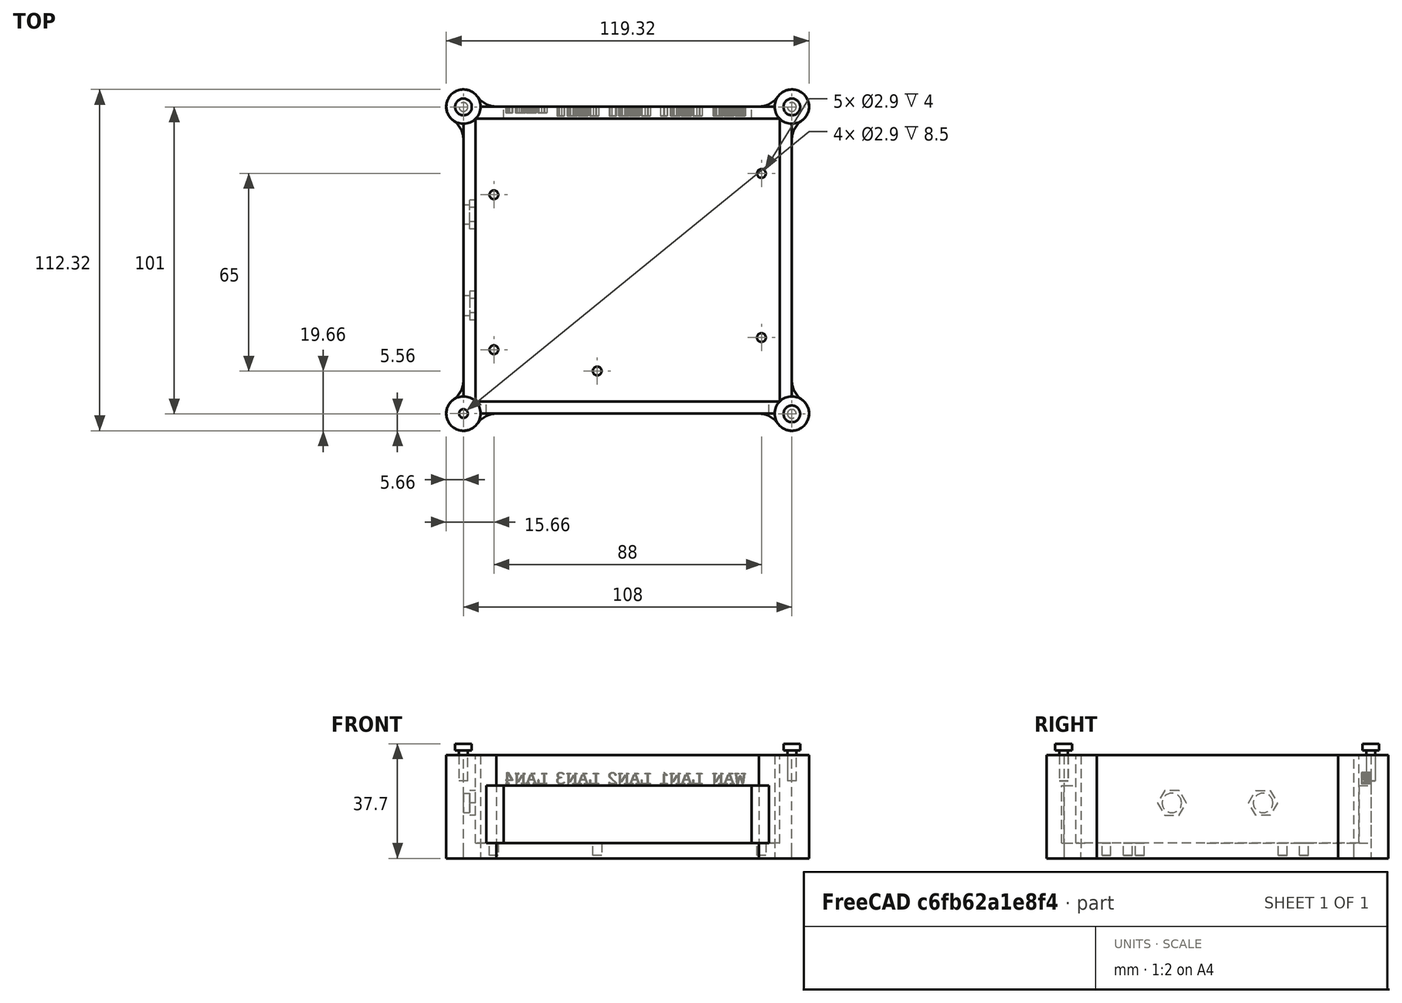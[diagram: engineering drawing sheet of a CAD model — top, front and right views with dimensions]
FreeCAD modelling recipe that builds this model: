
FCSTD DOCUMENT  (FreeCAD 2023.521R14555 (Git shallow))
Label: HLK-7628N_case
License: All rights reserved
objects: PartDesign::SubShapeBinder×13, Sketcher::SketchObject×12, PartDesign::Pocket×10, PartDesign::Pad×8, PartDesign::Mirrored×6, PartDesign::Body×5, Part::Part2DObjectPython×5, PartDesign::FeatureBase×3, PartDesign::MultiTransform×2, PartDesign::Plane×2, PartDesign::Boolean×2
note: 137 computed .brp shape members not serialized (recipe doc carries the construction recipe); baked Part::Feature solids carry a one-line shape summary decoded from their .brp

FEATURE [Sketcher::SketchObject] Sketch
  ArcFitTolerance = 1e-06
  AttachmentSupport = -> [XY_Plane]
  ExternalBSplineMaxDegree = 5
  ExternalBSplineTolerance = 0.0001
  FullyConstrained = true
  InternalTolerance = 1e-06
  InvalidShape = false
  MakeInternals = false
  MapMode = 5
  Support = -> [XY_Plane]
  TreeRank = 11
  ValidateShape = true
  sketch-geometry (4):
    g0: LineSegment StartX=-50 StartY=46.5 StartZ=0 EndX=50 EndY=46.5 EndZ=0
    g1: LineSegment StartX=50 StartY=46.5 StartZ=0 EndX=50 EndY=-46.5 EndZ=0
    g2: LineSegment StartX=50 StartY=-46.5 StartZ=0 EndX=-50 EndY=-46.5 EndZ=0
    g3: LineSegment StartX=-50 StartY=-46.5 StartZ=0 EndX=-50 EndY=46.5 EndZ=0
  constraints (11):
    c: Coincident(g0,g1)
    c: Coincident(g1,g2)
    c: Coincident(g2,g3)
    c: Coincident(g3,g0)
    c: Horizontal(g0)
    c: Horizontal(g2)
    c: Vertical(g1)
    c: Vertical(g3)
    c: Symmetric(g0,g1,g-1)
    c: DistanceX(g2,g2) = 100
    c: DistanceY(g3,g3) = 93
FEATURE [PartDesign::Pad] Pad
  AddSubType = 0
  AlongSketchNormal = false
  AutoTaperInnerAngle = true
  CheckUpToFaceLimits = true
  ClaimChildren = false
  Direction = (0,0,1)
  Fit = 0
  FitJoin = 0
  InnerFit = 0
  InnerFitJoin = 0
  InvalidShape = false
  Length = 5
  Length2 = 100
  Linearize = true
  NewSolid = false
  Profile = -> Sketch
  Suppress = false
  TaperInnerAngle = 0
  TaperInnerAngleRev = 0
  TreeRank = 12
  Type = 0
  ValidateShape = true
  _ProfileBasedVersion = 1
FEATURE [Sketcher::SketchObject] Sketch001
  ArcFitTolerance = 1e-06
  AttachmentSupport = -> [Pad]
  ExternalBSplineMaxDegree = 5
  ExternalBSplineTolerance = 0.0001
  ExternalGeometry = -> [Pad]
  FullyConstrained = true
  InternalTolerance = 1e-06
  InvalidShape = false
  MakeInternals = false
  MapMode = 5
  Placement = pos=(0,0,0) rot=(1,0,0;3.14159rad)
  Support = -> [Pad]
  TreeRank = 13
  ValidateShape = true
  sketch-geometry (12):
    g0: LineSegment StartX=-54 StartY=-50.5 StartZ=0 EndX=54 EndY=-50.5 EndZ=0
    g1: LineSegment StartX=54 StartY=-50.5 StartZ=0 EndX=54 EndY=50.5 EndZ=0
    g2: LineSegment StartX=54 StartY=50.5 StartZ=0 EndX=-54 EndY=50.5 EndZ=0
    g3: LineSegment StartX=-54 StartY=50.5 StartZ=0 EndX=-54 EndY=-50.5 EndZ=0
    g4: LineSegment [constr] StartX=-50 StartY=46.5 StartZ=0 EndX=-50 EndY=50.5 EndZ=0
    g5: LineSegment [constr] StartX=-50 StartY=46.5 StartZ=0 EndX=-54 EndY=46.5 EndZ=0
    g6: LineSegment StartX=-50 StartY=-46.5 StartZ=0 EndX=50 EndY=-46.5 EndZ=0
    g7: LineSegment StartX=50 StartY=-46.5 StartZ=0 EndX=50 EndY=46.5 EndZ=0
    g8: LineSegment StartX=50 StartY=46.5 StartZ=0 EndX=-50 EndY=46.5 EndZ=0
    g9: LineSegment StartX=-50 StartY=46.5 StartZ=0 EndX=-50 EndY=-46.5 EndZ=0
    g10: LineSegment [constr] StartX=50 StartY=-46.5 StartZ=0 EndX=54 EndY=-46.5 EndZ=0
    g11: LineSegment [constr] StartX=50 StartY=-46.5 StartZ=0 EndX=50 EndY=-50.5 EndZ=0
  constraints (34):
    c: Coincident(g0,g1)
    c: Coincident(g1,g2)
    c: Coincident(g2,g3)
    c: Coincident(g3,g0)
    c: Horizontal(g0)
    c: Horizontal(g2)
    c: Vertical(g1)
    c: Vertical(g3)
    c: Coincident(g4,g-6)
    c: PointOnObject(g4,g2)
    c: Vertical(g4)
    c: Coincident(g5,g-6)
    c: PointOnObject(g5,g3)
    c: Horizontal(g5)
    c: Equal(g5,g4)
    c: Coincident(g6,g7)
    c: Coincident(g7,g8)
    c: Coincident(g8,g9)
    c: Coincident(g9,g6)
    c: Horizontal(g6)
    c: Horizontal(g8)
    c: Vertical(g7)
    c: Vertical(g9)
    c: Coincident(g6,g-5)
    c: Coincident(g7,g-6)
    c: DistanceX(g5,g5) = 4
    c: Coincident(g10,g6)
    c: PointOnObject(g10,g1)
    c: Horizontal(g10)
    c: Coincident(g11,g6)
    c: PointOnObject(g11,g0)
    c: Vertical(g11)
    c: Equal(g10,g11)
    c: Equal(g10,g4)
FEATURE [PartDesign::Pad] Pad001
  AddSubType = 0
  AlongSketchNormal = false
  AutoTaperInnerAngle = true
  BaseFeature = -> Pad
  CheckUpToFaceLimits = true
  ClaimChildren = false
  Direction = (0,0,-1)
  Fit = 0
  FitJoin = 0
  InnerFit = 0
  InnerFitJoin = 0
  InvalidShape = false
  Length = 34
  Length2 = 100
  Linearize = true
  NewSolid = false
  Profile = -> Sketch001
  Reversed = true
  Suppress = false
  TaperInnerAngle = 0
  TaperInnerAngleRev = 0
  TreeRank = 14
  Type = 0
  ValidateShape = true
  _ProfileBasedVersion = 1
FEATURE [Sketcher::SketchObject] Sketch002
  ArcFitTolerance = 1e-06
  AttachmentSupport = -> [Pad001]
  ExternalBSplineMaxDegree = 5
  ExternalBSplineTolerance = 0.0001
  ExternalGeometry = -> [Pad001]
  FullyConstrained = true
  InternalTolerance = 1e-06
  InvalidShape = false
  MakeInternals = false
  MapMode = 5
  Placement = pos=(0,46.5,0) rot=(1,0,0;1.5708rad)
  Support = -> [Pad001]
  TreeRank = 15
  ValidateShape = true
  sketch-geometry (4):
    g0: LineSegment StartX=40.75 StartY=5 StartZ=0 EndX=-40.75 EndY=5 EndZ=0
    g1: LineSegment StartX=-40.75 StartY=5 StartZ=0 EndX=-40.75 EndY=24 EndZ=0
    g2: LineSegment StartX=-40.75 StartY=24 StartZ=0 EndX=40.75 EndY=24 EndZ=0
    g3: LineSegment StartX=40.75 StartY=24 StartZ=0 EndX=40.75 EndY=5 EndZ=0
  constraints (11):
    c: Coincident(g0,g1)
    c: Coincident(g1,g2)
    c: Coincident(g2,g3)
    c: Coincident(g3,g0)
    c: Horizontal(g2)
    c: Vertical(g1)
    c: Vertical(g3)
    c: PointOnObject(g0,g-3)
    c: Symmetric(g0,g0,g-2)
    c: DistanceX(g0,g0) = 81.5
    c: DistanceY(g1,g1) = 19
FEATURE [PartDesign::Mirrored] Mirrored001
  AddSubType = 0
  CopyShape = false
  InvalidShape = false
  MirrorPlane = -> YZ_Plane
  NewSolid = false
  ParallelTransform = true
  SubTransform = true
  Suppress = false
  TreeRank = 27
  ValidateShape = true
  _Version = 3
FEATURE [PartDesign::Mirrored] Mirrored002
  AddSubType = 0
  CopyShape = false
  InvalidShape = false
  MirrorPlane = -> XZ_Plane
  NewSolid = false
  ParallelTransform = true
  SubTransform = true
  Suppress = false
  TreeRank = 28
  ValidateShape = true
  _Version = 3
FEATURE [Sketcher::SketchObject] Sketch008
  ArcFitTolerance = 1e-06
  AttachmentSupport = -> [XY_Plane001]
  ExternalBSplineMaxDegree = 5
  ExternalBSplineTolerance = 0.0001
  FullyConstrained = true
  InternalTolerance = 1e-06
  InvalidShape = false
  MakeInternals = false
  MapMode = 5
  Support = -> [XY_Plane001]
  TreeRank = 52
  ValidateShape = false
  sketch-geometry (1):
    g0: Circle CenterX=0 CenterY=0 CenterZ=0 NormalX=0 NormalY=0 NormalZ=1 AngleXU=0 Radius=1.45
  constraints (2):
    c: Coincident(g0,g-1)
    c: Diameter(g0) = 2.9
FEATURE [PartDesign::Pad] Pad004
  AddSubType = 0
  AlongSketchNormal = false
  AutoTaperInnerAngle = true
  CheckUpToFaceLimits = true
  ClaimChildren = false
  Direction = (0,0,1)
  Fit = 0
  FitJoin = 0
  InnerFit = 0
  InnerFitJoin = 0
  InvalidShape = false
  Length = 10
  Length2 = 10
  Linearize = true
  NewSolid = false
  Profile = -> Sketch008
  ReferenceAxis = -> Sketch008 [N_Axis]
  Suppress = false
  TaperInnerAngle = 0
  TaperInnerAngleRev = 0
  TreeRank = 53
  Type = 0
  ValidateShape = false
  _ProfileBasedVersion = 1
FEATURE [Sketcher::SketchObject] Sketch009
  ArcFitTolerance = 1e-06
  AttachmentSupport = -> [Pad004]
  ExternalBSplineMaxDegree = 5
  ExternalBSplineTolerance = 0.0001
  FullyConstrained = true
  InternalTolerance = 1e-06
  InvalidShape = false
  MakeInternals = false
  MapMode = 5
  Placement = pos=(0,0,10) rot=(0,0,1;0rad)
  Support = -> [Pad004]
  TreeRank = 54
  ValidateShape = false
  sketch-geometry (1):
    g0: Circle CenterX=0 CenterY=0 CenterZ=0 NormalX=0 NormalY=0 NormalZ=1 AngleXU=0 Radius=2.75
  constraints (2):
    c: Coincident(g0,g-1)
    c: Diameter(g0) = 5.5
FEATURE [PartDesign::Pad] Pad005
  AddSubType = 0
  AlongSketchNormal = false
  AutoTaperInnerAngle = true
  BaseFeature = -> Pad004
  CheckUpToFaceLimits = true
  ClaimChildren = false
  Direction = (0,0,1)
  Fit = 0
  FitJoin = 0
  InnerFit = 0
  InnerFitJoin = 0
  InvalidShape = false
  Length = 2.2
  Length2 = 10
  Linearize = true
  NewSolid = false
  Profile = -> Sketch009
  ReferenceAxis = -> Sketch009 [N_Axis]
  Suppress = false
  TaperInnerAngle = 0
  TaperInnerAngleRev = 0
  TreeRank = 55
  Type = 0
  ValidateShape = false
  _ProfileBasedVersion = 1
FEATURE [PartDesign::Body] Body001  label="M3_10"
  AutoGroupSolids = false
  ClaimAllChildren = false
  ExportMode = 0
  Group = -> [Sketch008,Pad004,Sketch009,Pad005]
  InvalidShape = false
  Origin = -> Origin001
  Placement = pos=(-54,-50.5,25.5) rot=(0,0,1;0rad)
  Tip = -> Pad005
  TreeRank = 56
  ValidateShape = false
  _ExportChildren = -> [Pad004,Pad005]
  _GroupVersion = 1
FEATURE [PartDesign::SubShapeBinder] Pocket006_Profile  label="Pocket006_Profile(WAN)"
  BindCopyOnChange = 0
  BindMode = 0
  ClaimChildren = false
  Context = -> Body [Pocket006_Profile.]
  EdgeTolerance = 1e-06
  FillStyle = 0
  Fuse = false
  InvalidShape = false
  MakeFace = true
  MergeEdges = true
  OffsetFill = false
  OffsetIntersection = false
  OffsetJoinType = 0
  OffsetOpenResult = false
  Outline = false
  PartialLoad = false
  Relative = true
  SplitEdges = false
  Support = -> [ShapeString]
  TightBound = false
  TreeRank = 74
  ValidateShape = false
  _Version = 8
FEATURE [PartDesign::SubShapeBinder] Pocket007_Profile  label="Pocket007_Profile(LAN1)"
  BindCopyOnChange = 0
  BindMode = 0
  ClaimChildren = false
  Context = -> Body [Pocket007_Profile.]
  EdgeTolerance = 1e-06
  FillStyle = 0
  Fuse = false
  InvalidShape = false
  MakeFace = true
  MergeEdges = true
  OffsetFill = false
  OffsetIntersection = false
  OffsetJoinType = 0
  OffsetOpenResult = false
  Outline = false
  PartialLoad = false
  Relative = true
  SplitEdges = false
  Support = -> [ShapeString001]
  TightBound = false
  TreeRank = 76
  ValidateShape = false
  _Version = 8
FEATURE [PartDesign::SubShapeBinder] Pocket008_Profile  label="Pocket008_Profile(LAN2)"
  BindCopyOnChange = 0
  BindMode = 0
  ClaimChildren = false
  Context = -> Body [Pocket008_Profile.]
  EdgeTolerance = 1e-06
  FillStyle = 0
  Fuse = false
  InvalidShape = false
  MakeFace = true
  MergeEdges = true
  OffsetFill = false
  OffsetIntersection = false
  OffsetJoinType = 0
  OffsetOpenResult = false
  Outline = false
  PartialLoad = false
  Relative = true
  SplitEdges = false
  Support = -> [ShapeString002]
  TightBound = false
  TreeRank = 78
  ValidateShape = false
  _Version = 8
FEATURE [PartDesign::SubShapeBinder] Pocket009_Profile  label="Pocket009_Profile(LAN3)"
  BindCopyOnChange = 0
  BindMode = 0
  ClaimChildren = false
  Context = -> Body [Pocket009_Profile.]
  EdgeTolerance = 1e-06
  FillStyle = 0
  Fuse = false
  InvalidShape = false
  MakeFace = true
  MergeEdges = true
  OffsetFill = false
  OffsetIntersection = false
  OffsetJoinType = 0
  OffsetOpenResult = false
  Outline = false
  PartialLoad = false
  Relative = true
  SplitEdges = false
  Support = -> [ShapeString003]
  TightBound = false
  TreeRank = 80
  ValidateShape = false
  _Version = 8
FEATURE [PartDesign::SubShapeBinder] Pocket010_Profile  label="Pocket010_Profile(LAN4)"
  BindCopyOnChange = 0
  BindMode = 0
  ClaimChildren = false
  Context = -> Body [Pocket010_Profile.]
  EdgeTolerance = 1e-06
  FillStyle = 0
  Fuse = false
  InvalidShape = false
  MakeFace = true
  MergeEdges = true
  OffsetFill = false
  OffsetIntersection = false
  OffsetJoinType = 0
  OffsetOpenResult = false
  Outline = false
  PartialLoad = false
  Relative = true
  SplitEdges = false
  Support = -> [ShapeString004]
  TightBound = false
  TreeRank = 82
  ValidateShape = false
  _Version = 8
FEATURE [PartDesign::Mirrored] Mirrored004
  AddSubType = 0
  CopyShape = false
  InvalidShape = false
  MirrorPlane = -> YZ_Plane
  NewSolid = false
  ParallelTransform = true
  SubTransform = true
  Suppress = false
  TreeRank = 89
  ValidateShape = true
  _Version = 3
FEATURE [PartDesign::Mirrored] Mirrored005
  AddSubType = 0
  CopyShape = false
  InvalidShape = false
  MirrorPlane = -> XZ_Plane
  NewSolid = false
  ParallelTransform = true
  SubTransform = true
  Suppress = false
  TreeRank = 90
  ValidateShape = true
  _Version = 3
FEATURE [PartDesign::FeatureBase] Clone
  BaseFeature = -> Body001
  InvalidShape = false
  NewSolid = false
  Placement = pos=(-54,-50.6,25.5) rot=(0,0,1;0rad)
  Suppress = false
  TreeRank = 108
  ValidateShape = true
FEATURE [PartDesign::Body] Body002
  AutoGroupSolids = false
  BaseFeature = -> Body001
  ClaimAllChildren = false
  ExportMode = 0
  Group = -> [Clone]
  InvalidShape = false
  Origin = -> Origin002
  Placement = pos=(0,101,0) rot=(0,0,1;0rad)
  Tip = -> Clone
  TreeRank = 109
  ValidateShape = false
  _ExportChildren = -> [Clone]
  _GroupVersion = 1
FEATURE [PartDesign::FeatureBase] Clone001
  BaseFeature = -> Body001
  InvalidShape = false
  NewSolid = false
  Placement = pos=(-54,-50.6,25.5) rot=(0,0,1;0rad)
  Suppress = false
  TreeRank = 119
  ValidateShape = true
FEATURE [PartDesign::Body] Body003
  AutoGroupSolids = false
  BaseFeature = -> Body001
  ClaimAllChildren = false
  ExportMode = 0
  Group = -> [Clone001]
  InvalidShape = false
  Origin = -> Origin003
  Placement = pos=(108,0,0) rot=(0,0,1;0rad)
  Tip = -> Clone001
  TreeRank = 120
  ValidateShape = false
  _ExportChildren = -> [Clone001]
  _GroupVersion = 1
FEATURE [PartDesign::FeatureBase] Clone002
  BaseFeature = -> Body001
  InvalidShape = false
  NewSolid = false
  Placement = pos=(-54,-50.6,25.5) rot=(0,0,1;0rad)
  Suppress = false
  TreeRank = 130
  ValidateShape = true
FEATURE [PartDesign::Body] Body004
  AutoGroupSolids = false
  BaseFeature = -> Body001
  ClaimAllChildren = false
  ExportMode = 0
  Group = -> [Clone002]
  InvalidShape = false
  Origin = -> Origin004
  Placement = pos=(108,101,0) rot=(0,0,1;0rad)
  Tip = -> Clone002
  TreeRank = 131
  ValidateShape = false
  _ExportChildren = -> [Clone002]
  _GroupVersion = 1
FEATURE [PartDesign::SubShapeBinder] Reference  label="Reference(M3_10)"
  BindCopyOnChange = 0
  BindMode = 0
  ClaimChildren = false
  Context = -> Body [Boolean.Reference.]
  EdgeTolerance = 1e-06
  FillStyle = 0
  Fuse = false
  InvalidShape = false
  MakeFace = true
  MergeEdges = true
  OffsetFill = false
  OffsetIntersection = false
  OffsetJoinType = 0
  OffsetOpenResult = false
  Outline = false
  PartialLoad = false
  Placement = pos=(0,0.5,0) rot=(0,0,1;0rad)
  Relative = true
  SplitEdges = false
  Support = -> [Body001]
  TightBound = false
  TreeRank = 137
  ValidateShape = false
  _Version = 8
FEATURE [PartDesign::SubShapeBinder] Reference001  label="Reference001(Body002)"
  BindCopyOnChange = 0
  BindMode = 0
  ClaimChildren = false
  Context = -> Body [Boolean.Reference001.]
  EdgeTolerance = 1e-06
  FillStyle = 0
  Fuse = false
  InvalidShape = false
  MakeFace = true
  MergeEdges = true
  OffsetFill = false
  OffsetIntersection = false
  OffsetJoinType = 0
  OffsetOpenResult = false
  Outline = false
  PartialLoad = false
  Relative = true
  SplitEdges = false
  Support = -> [Body002]
  TightBound = false
  TreeRank = 138
  ValidateShape = false
  _Version = 8
FEATURE [PartDesign::SubShapeBinder] Reference002  label="Reference002(Body003)"
  BindCopyOnChange = 0
  BindMode = 0
  ClaimChildren = false
  Context = -> Body [Boolean.Reference002.]
  EdgeTolerance = 1e-06
  FillStyle = 0
  Fuse = false
  InvalidShape = false
  MakeFace = true
  MergeEdges = true
  OffsetFill = false
  OffsetIntersection = false
  OffsetJoinType = 0
  OffsetOpenResult = false
  Outline = false
  PartialLoad = false
  Relative = true
  SplitEdges = false
  Support = -> [Body003]
  TightBound = false
  TreeRank = 139
  ValidateShape = false
  _Version = 8
FEATURE [PartDesign::SubShapeBinder] Reference003  label="Reference003(Body004)"
  BindCopyOnChange = 0
  BindMode = 0
  ClaimChildren = false
  Context = -> Body [Boolean.Reference003.]
  EdgeTolerance = 1e-06
  FillStyle = 0
  Fuse = false
  InvalidShape = false
  MakeFace = true
  MergeEdges = true
  OffsetFill = false
  OffsetIntersection = false
  OffsetJoinType = 0
  OffsetOpenResult = false
  Outline = false
  PartialLoad = false
  Relative = true
  SplitEdges = false
  Support = -> [Body004]
  TightBound = false
  TreeRank = 140
  ValidateShape = false
  _Version = 8
FEATURE [PartDesign::SubShapeBinder] Reference004  label="Reference004(M3_10)"
  BindCopyOnChange = 0
  BindMode = 0
  ClaimChildren = false
  Context = -> Body [Boolean001.Reference004.]
  EdgeTolerance = 1e-06
  FillStyle = 0
  Fuse = false
  InvalidShape = false
  MakeFace = true
  MergeEdges = true
  OffsetFill = false
  OffsetIntersection = false
  OffsetJoinType = 0
  OffsetOpenResult = false
  Outline = false
  PartialLoad = false
  Relative = true
  SplitEdges = false
  Support = -> [Body001]
  TightBound = false
  TreeRank = 146
  ValidateShape = false
  _Version = 8
FEATURE [PartDesign::SubShapeBinder] Reference005  label="Reference005(Body002)"
  BindCopyOnChange = 0
  BindMode = 0
  ClaimChildren = false
  Context = -> Body [Boolean001.Reference005.]
  EdgeTolerance = 1e-06
  FillStyle = 0
  Fuse = false
  InvalidShape = false
  MakeFace = true
  MergeEdges = true
  OffsetFill = false
  OffsetIntersection = false
  OffsetJoinType = 0
  OffsetOpenResult = false
  Outline = false
  PartialLoad = false
  Relative = true
  SplitEdges = false
  Support = -> [Body002]
  TightBound = false
  TreeRank = 147
  ValidateShape = false
  _Version = 8
FEATURE [PartDesign::SubShapeBinder] Reference006  label="Reference006(Body003)"
  BindCopyOnChange = 0
  BindMode = 0
  ClaimChildren = false
  Context = -> Body [Boolean001.Reference006.]
  EdgeTolerance = 1e-06
  FillStyle = 0
  Fuse = false
  InvalidShape = false
  MakeFace = true
  MergeEdges = true
  OffsetFill = false
  OffsetIntersection = false
  OffsetJoinType = 0
  OffsetOpenResult = false
  Outline = false
  PartialLoad = false
  Relative = true
  SplitEdges = false
  Support = -> [Body003]
  TightBound = false
  TreeRank = 148
  ValidateShape = false
  _Version = 8
FEATURE [PartDesign::SubShapeBinder] Reference007  label="Reference007(Body004)"
  BindCopyOnChange = 0
  BindMode = 0
  ClaimChildren = false
  Context = -> Body [Boolean001.Reference007.]
  EdgeTolerance = 1e-06
  FillStyle = 0
  Fuse = false
  InvalidShape = false
  MakeFace = true
  MergeEdges = true
  OffsetFill = false
  OffsetIntersection = false
  OffsetJoinType = 0
  OffsetOpenResult = false
  Outline = false
  PartialLoad = false
  Relative = true
  SplitEdges = false
  Support = -> [Body004]
  TightBound = false
  TreeRank = 149
  ValidateShape = false
  _Version = 8
FEATURE [PartDesign::Body] Body  label="Bottom"
  AutoGroupSolids = false
  ClaimAllChildren = false
  ExportMode = 0
  Group = -> [Sketch,Pad,Sketch001,Pad001,Sketch002,Sketch004,Sketch011,Pocket002,Sketch005,Pocket003,Mirrored,Sketch006,Pad002,MultiTransform,Mirrored001,Mirrored002,Sketch012,Pad006,MultiTransform001,Pocket,Pocket005,Mirrored003,Pocket006_Profile,Pocket007_Profile,Pocket008_Profile,Pocket009_Profile,Pocket010_Profile,DatumPlane,Mirrored004,Mirrored005,Boolean001,Pocket006,Pocket007,Pocket008,Pocket009,+7 more]
  InvalidShape = false
  Origin = -> Origin
  Tip = -> Pocket011
  TreeRank = 10
  ValidateShape = true
  _ExportChildren = -> [Pad,Pad001,Pocket002,Pocket003,Mirrored,Pad002,MultiTransform,Pad006,MultiTransform001,Pocket,Pocket005,DatumPlane,Boolean001,Pocket006,Pocket007,Pocket008,Pocket009,Pocket010,Pad008,Pocket011,Pad007,Boolean]
  _GroupVersion = 1
FEATURE [PartDesign::Pocket] Pocket
  AddSubType = 1
  AlongSketchNormal = false
  AutoTaperInnerAngle = true
  BaseFeature = -> MultiTransform001
  CheckUpToFaceLimits = true
  ClaimChildren = false
  Direction = (0,1,-2e-16)
  Fit = 0
  FitJoin = 0
  InnerFit = 0
  InnerFitJoin = 0
  InvalidShape = false
  Length = 0
  Length2 = 100
  Linearize = true
  Midplane = true
  NewSolid = false
  Profile = -> Sketch002
  Suppress = false
  TaperInnerAngle = 0
  TaperInnerAngleRev = 0
  TreeRank = 16
  Type = 4
  ValidateShape = true
  _ProfileBasedVersion = 1
  _Version = 1
FEATURE [PartDesign::Pocket] Pocket002
  AddSubType = 1
  AutoTaperInnerAngle = true
  BaseFeature = -> Pad001
  CheckUpToFaceLimits = true
  ClaimChildren = false
  Direction = (-1,0,0)
  Fit = 0
  FitJoin = 0
  InnerFit = 0
  InnerFitJoin = 0
  InvalidShape = false
  Length = 2
  Length2 = 100
  Linearize = true
  NewSolid = false
  Profile = -> Sketch004
  Suppress = false
  TaperInnerAngle = 0
  TaperInnerAngleRev = 0
  TreeRank = 20
  Type = 0
  ValidateShape = true
  _ProfileBasedVersion = 1
  _Version = 1
FEATURE [Sketcher::SketchObject] Sketch005
  ArcFitTolerance = 1e-06
  AttachmentSupport = -> [Pocket002]
  ExternalBSplineMaxDegree = 5
  ExternalBSplineTolerance = 0.0001
  ExternalGeometry = -> [Pocket002]
  FullyConstrained = true
  InternalTolerance = 1e-06
  InvalidShape = false
  MakeInternals = false
  MapMode = 5
  Placement = pos=(-52,0,0) rot=(0.57735,0.57735,0.57735;2.0944rad)
  Support = -> [Pocket002]
  TreeRank = 21
  ValidateShape = true
  sketch-geometry (3):
    g0: LineSegment [constr] StartX=-12.6329 StartY=22.3432 StartZ=0 EndX=-17.3671 EndY=14.1432 EndZ=0
    g1: GeomPoint [constr] X=-15 Y=18.2432 Z=0
    g2: Circle CenterX=-15 CenterY=18.2432 CenterZ=0 NormalX=0 NormalY=0 NormalZ=1 AngleXU=0 Radius=3.2
  constraints (5):
    c: Coincident(g0,g-3)
    c: Coincident(g0,g-4)
    c: Symmetric(g-3,g-4,g1)
    c: Coincident(g2,g1)
    c: Diameter(g2) = 6.4
FEATURE [PartDesign::Pocket] Pocket003
  AddSubType = 1
  AutoTaperInnerAngle = true
  BaseFeature = -> Pocket002
  CheckUpToFaceLimits = true
  ClaimChildren = false
  Direction = (-1,0,0)
  Fit = 0
  FitJoin = 0
  InnerFit = 0
  InnerFitJoin = 0
  InvalidShape = false
  Length = 0
  Length2 = 100
  Linearize = true
  NewSolid = false
  Profile = -> Sketch005
  Suppress = false
  TaperInnerAngle = 0
  TaperInnerAngleRev = 0
  TreeRank = 22
  Type = 3
  UpToFace = -> Pocket002 [Face6]
  ValidateShape = true
  _ProfileBasedVersion = 1
  _Version = 1
FEATURE [PartDesign::Mirrored] Mirrored
  AddSubType = 0
  BaseFeature = -> Pocket003
  CopyShape = false
  InvalidShape = false
  MirrorPlane = -> XZ_Plane
  NewSolid = false
  OriginalSubs = -> [Pocket002,Pocket003]
  Originals = -> [Pocket002,Pocket003]
  ParallelTransform = true
  SubTransform = true
  Suppress = false
  TreeRank = 23
  ValidateShape = true
  _Version = 3
FEATURE [Sketcher::SketchObject] Sketch006
  ArcFitTolerance = 1e-06
  AttachmentSupport = -> [Mirrored]
  ExternalBSplineMaxDegree = 5
  ExternalBSplineTolerance = 0.0001
  ExternalGeometry = -> [Mirrored]
  FullyConstrained = true
  InternalTolerance = 1e-06
  InvalidShape = false
  MakeInternals = false
  MapMode = 5
  Placement = pos=(0,0,34) rot=(0,0,1;0rad)
  Support = -> [Mirrored]
  TreeRank = 24
  ValidateShape = true
  sketch-geometry (1):
    g0: Circle CenterX=-54 CenterY=50.5 CenterZ=0 NormalX=0 NormalY=0 NormalZ=1 AngleXU=0 Radius=5.65685
  constraints (2):
    c: Coincident(g0,g-3)
    c: PointOnObject(g-4,g0)
FEATURE [PartDesign::Pad] Pad002
  AddSubType = 0
  AlongSketchNormal = false
  AutoTaperInnerAngle = true
  BaseFeature = -> Mirrored
  CheckUpToFaceLimits = true
  ClaimChildren = false
  Direction = (0,0,1)
  Fit = 0
  FitJoin = 0
  InnerFit = 0
  InnerFitJoin = 0
  InvalidShape = false
  Length = 10
  Length2 = 100
  Linearize = true
  NewSolid = false
  Profile = -> Sketch006
  Suppress = false
  TaperInnerAngle = 0
  TaperInnerAngleRev = 0
  TreeRank = 25
  Type = 3
  UpToFace = -> Mirrored [Face2]
  ValidateShape = true
  _ProfileBasedVersion = 1
FEATURE [PartDesign::MultiTransform] MultiTransform
  AddSubType = 0
  BaseFeature = -> Pad002
  CopyShape = false
  InvalidShape = false
  NewSolid = false
  OriginalSubs = -> [Pad002]
  Originals = -> [Pad002]
  ParallelTransform = true
  SubTransform = true
  Suppress = false
  Transformations = -> [Mirrored001,Mirrored002]
  TreeRank = 26
  ValidateShape = true
  _Version = 3
FEATURE [Sketcher::SketchObject] Sketch004
  ArcFitTolerance = 1e-06
  AttachmentSupport = -> [Pocket]
  ExternalBSplineMaxDegree = 5
  ExternalBSplineTolerance = 0.0001
  ExternalGeometry = -> [Pocket]
  FullyConstrained = false
  InternalTolerance = 1e-06
  InvalidShape = false
  MakeInternals = false
  MapMode = 5
  Placement = pos=(-50,0,0) rot=(0.57735,0.57735,0.57735;2.0944rad)
  Support = -> [Pocket]
  TreeRank = 67
  ValidateShape = true
  sketch-geometry (7):
    g0: LineSegment StartX=-10.2657 StartY=18.2432 StartZ=0 EndX=-12.6329 EndY=22.3432 EndZ=0
    g1: LineSegment StartX=-12.6329 StartY=22.3432 StartZ=0 EndX=-17.3671 EndY=22.3432 EndZ=0
    g2: LineSegment StartX=-17.3671 StartY=22.3432 StartZ=0 EndX=-19.7343 EndY=18.2432 EndZ=0
    g3: LineSegment StartX=-19.7343 StartY=18.2432 StartZ=0 EndX=-17.3671 EndY=14.1432 EndZ=0
    g4: LineSegment StartX=-17.3671 StartY=14.1432 StartZ=0 EndX=-12.6329 EndY=14.1432 EndZ=0
    g5: LineSegment StartX=-12.6329 StartY=14.1432 StartZ=0 EndX=-10.2657 EndY=18.2432 EndZ=0
    g6: Circle [constr] CenterX=-15 CenterY=18.2432 CenterZ=0 NormalX=0 NormalY=0 NormalZ=1 AngleXU=0 Radius=4.73427
  constraints (18):
    c: Coincident(g0,g1)
    c: Coincident(g1,g2)
    c: Coincident(g2,g3)
    c: Coincident(g3,g4)
    c: Coincident(g4,g5)
    c: Coincident(g5,g0)
    c: Equal(g0, g1-g5) x5
    c: PointOnObject(g0,g6)
    c: PointOnObject(g1,g6)
    c: PointOnObject(g2,g6)
    c: PointOnObject(g3,g6)
    c: PointOnObject(g4,g6)
    c: PointOnObject(g5,g6)
    c: Horizontal(g4)
    c: DistanceY(g4,g0) = 8.2
    c: DistanceY(g0,g-4) = 11.6568
    c: DistanceY(g-3,g4) = 9.14322
    c: DistanceX(g6,g-1) = 15
FEATURE [Sketcher::SketchObject] Sketch011
  ArcFitTolerance = 1e-06
  AttachmentSupport = -> [Pocket]
  ExternalBSplineMaxDegree = 5
  ExternalBSplineTolerance = 0.0001
  ExternalGeometry = -> [Pocket]
  FullyConstrained = true
  InternalTolerance = 1e-06
  InvalidShape = false
  MakeInternals = false
  MapMode = 5
  Placement = pos=(0,-50.5,0) rot=(1,0,0;1.5708rad)
  Support = -> [Pocket]
  TreeRank = 70
  ValidateShape = false
  sketch-geometry (4):
    g0: LineSegment StartX=-46.5 StartY=5 StartZ=0 EndX=46.5 EndY=5 EndZ=0
    g1: LineSegment StartX=46.5 StartY=5 StartZ=0 EndX=46.5 EndY=24 EndZ=0
    g2: LineSegment StartX=46.5 StartY=24 StartZ=0 EndX=-46.5 EndY=24 EndZ=0
    g3: LineSegment StartX=-46.5 StartY=24 StartZ=0 EndX=-46.5 EndY=5 EndZ=0
  constraints (11):
    c: Coincident(g0,g1)
    c: Coincident(g1,g2)
    c: Coincident(g2,g3)
    c: Coincident(g3,g0)
    c: Horizontal(g0)
    c: Vertical(g1)
    c: Vertical(g3)
    c: Symmetric(g2,g1,g-2)
    c: DistanceX(g2,g2) = 93
    c: DistanceY(g3,g3) = 19
    c: PointOnObject(g0,g-3)
FEATURE [PartDesign::Pocket] Pocket005  label="base"
  AddSubType = 1
  AlongSketchNormal = false
  AutoTaperInnerAngle = true
  BaseFeature = -> Pocket
  CheckUpToFaceLimits = true
  ClaimChildren = false
  Direction = (0,1,-2e-16)
  Fit = 0
  FitJoin = 0
  InnerFit = 0
  InnerFitJoin = 0
  InvalidShape = false
  Length = 8
  Length2 = 10
  Linearize = true
  NewSolid = false
  Profile = -> Sketch011
  ReferenceAxis = -> Sketch011 [N_Axis]
  Suppress = false
  TaperInnerAngle = 0
  TaperInnerAngleRev = 0
  TreeRank = 71
  Type = 4
  ValidateShape = true
  _ProfileBasedVersion = 1
  _Version = 1
FEATURE [Part::Part2DObjectPython] ShapeString  label="WAN"  # Draft 2D object (typed FeaturePython)
  AttachmentSupport = -> [MultiTransform]
  FontFile = <path>
  InvalidShape = false
  MakeFace = true
  Placement = pos=(38.83,50.5,24.52) rot=(0,0.707107,0.707107;3.14159rad)
  Size = 2
  String = WAN
  Support = -> [MultiTransform]
  Tracking = 0
  TreeRank = 72
  ValidateShape = false
FEATURE [Part::Part2DObjectPython] ShapeString001  label="LAN1"  # Draft 2D object (typed FeaturePython)
  AttachmentSupport = -> [MultiTransform]
  FontFile = <path>
  InvalidShape = false
  MakeFace = true
  Placement = pos=(24.83,50.5,24.52) rot=(0,0.707107,0.707107;3.14159rad)
  Size = 2
  String = LAN1
  Support = -> [MultiTransform]
  Tracking = 0
  TreeRank = 72
  ValidateShape = false
FEATURE [Part::Part2DObjectPython] ShapeString002  label="LAN2"  # Draft 2D object (typed FeaturePython)
  AttachmentSupport = -> [MultiTransform]
  FontFile = <path>
  InvalidShape = false
  MakeFace = true
  Placement = pos=(7.83,50.5,24.52) rot=(0,0.707107,0.707107;3.14159rad)
  Size = 2
  String = LAN2
  Support = -> [MultiTransform]
  Tracking = 0
  TreeRank = 72
  ValidateShape = false
FEATURE [Part::Part2DObjectPython] ShapeString003  label="LAN3"  # Draft 2D object (typed FeaturePython)
  AttachmentSupport = -> [MultiTransform]
  FontFile = <path>
  InvalidShape = false
  MakeFace = true
  Placement = pos=(-9.17,50.5,24.52) rot=(0,0.707107,0.707107;3.14159rad)
  Size = 2
  String = LAN3
  Support = -> [MultiTransform]
  Tracking = 0
  TreeRank = 72
  ValidateShape = false
FEATURE [Part::Part2DObjectPython] ShapeString004  label="LAN4"  # Draft 2D object (typed FeaturePython)
  AttachmentSupport = -> [MultiTransform]
  FontFile = <path>
  InvalidShape = false
  MakeFace = true
  Placement = pos=(-26.17,50.5,24.52) rot=(0,0.707107,0.707107;3.14159rad)
  Size = 2
  String = LAN4
  Support = -> [MultiTransform]
  Tracking = 0
  TreeRank = 72
  ValidateShape = false
FEATURE [Sketcher::SketchObject] Sketch012
  ArcFitTolerance = 1e-06
  AttachmentSupport = -> [MultiTransform]
  ExternalBSplineMaxDegree = 5
  ExternalBSplineTolerance = 0.0001
  ExternalGeometry = -> [MultiTransform]
  FullyConstrained = false
  InternalTolerance = 1e-06
  InvalidShape = false
  MakeInternals = false
  MapMode = 5
  Placement = pos=(-7.5e-15,0,34) rot=(0,0,1;0rad)
  Support = -> [MultiTransform]
  TreeRank = 84
  ValidateShape = false
  sketch-geometry (3):
    g0: ArcOfCircle CenterX=61.5774 CenterY=39.6497 CenterZ=0 NormalX=0 NormalY=0 NormalZ=1 AngleXU=0 Radius=7.57736 StartAngle=2.18042 EndAngle=3.14159
    g1: LineSegment StartX=54 StartY=44.8431 StartZ=0 EndX=54 EndY=39.6497 EndZ=0
    g2: ArcOfCircle CenterX=54 CenterY=50.5 CenterZ=0 NormalX=0 NormalY=0 NormalZ=1 AngleXU=0 Radius=5.65685 StartAngle=4.71239 EndAngle=5.32201
  constraints (7):
    c: Tangent(g0,g-4) = -1.5708
    c: Coincident(g1,g0)
    c: Tangent(g0,g-3)
    c: Coincident(g2,g-3)
    c: Coincident(g2,g0)
    c: Coincident(g2,g1)
    c: PointOnObject(g1,g-3)
FEATURE [PartDesign::Pad] Pad006
  AddSubType = 0
  AlongSketchNormal = false
  AutoTaperInnerAngle = true
  BaseFeature = -> MultiTransform
  CheckUpToFaceLimits = true
  ClaimChildren = false
  Direction = (-2e-16,0,1)
  Fit = 0
  FitJoin = 0
  InnerFit = 0
  InnerFitJoin = 0
  InvalidShape = false
  Length = 10
  Length2 = 10
  Linearize = true
  NewSolid = false
  Profile = -> Sketch012
  ReferenceAxis = -> Sketch012 [N_Axis]
  Suppress = false
  TaperInnerAngle = 0
  TaperInnerAngleRev = 0
  TreeRank = 85
  Type = 3
  UpToFace = -> MultiTransform [Face17]
  ValidateShape = true
  _ProfileBasedVersion = 1
FEATURE [PartDesign::Plane] DatumPlane
  AttachmentSupport = -> [Pad006]
  InvalidShape = false
  Length = 163.774
  MapMode = 13
  MinimumLength = 10
  MinimumWidth = 10
  Placement = pos=(52.6667,49.1667,22.6667) rot=(-0.281085,0.678598,0.678598;3.68962rad)
  ResizeMode = 0
  Support = -> [Pad006]
  TreeRank = 86
  ValidateShape = false
  Width = 34
FEATURE [PartDesign::Mirrored] Mirrored003
  AddSubType = 0
  CopyShape = false
  InvalidShape = false
  MirrorPlane = -> DatumPlane
  NewSolid = false
  ParallelTransform = true
  SubTransform = true
  Suppress = false
  TreeRank = 87
  ValidateShape = true
  _Version = 3
FEATURE [PartDesign::MultiTransform] MultiTransform001  label="Fillets"
  AddSubType = 0
  BaseFeature = -> Pad006
  CopyShape = false
  InvalidShape = false
  NewSolid = false
  OriginalSubs = -> [Pad006]
  Originals = -> [Pad006]
  ParallelTransform = true
  SubTransform = true
  Suppress = false
  Transformations = -> [Mirrored003,Mirrored004,Mirrored005]
  TreeRank = 88
  ValidateShape = true
  _Version = 3
FEATURE [PartDesign::Pocket] Pocket006
  AddSubType = 1
  AlongSketchNormal = false
  AutoTaperInnerAngle = true
  BaseFeature = -> Boolean001
  CheckUpToFaceLimits = true
  ClaimChildren = false
  Direction = (-1e-16,-1,2e-16)
  Fit = 0
  FitJoin = 0
  InnerFit = 0
  InnerFitJoin = 0
  InvalidShape = false
  Length = 3
  Length2 = 10
  Linearize = true
  NewSolid = false
  Profile = -> Pocket006_Profile
  Suppress = false
  TaperInnerAngle = 0
  TaperInnerAngleRev = 0
  TreeRank = 91
  Type = 0
  ValidateShape = true
  _ProfileBasedVersion = 1
  _Version = 1
FEATURE [PartDesign::Pocket] Pocket007
  AddSubType = 1
  AlongSketchNormal = false
  AutoTaperInnerAngle = true
  BaseFeature = -> Pocket006
  CheckUpToFaceLimits = true
  ClaimChildren = false
  Direction = (-1e-16,-1,2e-16)
  Fit = 0
  FitJoin = 0
  InnerFit = 0
  InnerFitJoin = 0
  InvalidShape = false
  Length = 3
  Length2 = 10
  Linearize = true
  NewSolid = false
  Profile = -> Pocket007_Profile
  Suppress = false
  TaperInnerAngle = 0
  TaperInnerAngleRev = 0
  TreeRank = 92
  Type = 0
  ValidateShape = true
  _ProfileBasedVersion = 1
  _Version = 1
FEATURE [PartDesign::Pocket] Pocket008
  AddSubType = 1
  AlongSketchNormal = false
  AutoTaperInnerAngle = true
  BaseFeature = -> Pocket007
  CheckUpToFaceLimits = true
  ClaimChildren = false
  Direction = (-1e-16,-1,2e-16)
  Fit = 0
  FitJoin = 0
  InnerFit = 0
  InnerFitJoin = 0
  InvalidShape = false
  Length = 3
  Length2 = 10
  Linearize = true
  NewSolid = false
  Profile = -> Pocket008_Profile
  Suppress = false
  TaperInnerAngle = 0
  TaperInnerAngleRev = 0
  TreeRank = 93
  Type = 0
  ValidateShape = true
  _ProfileBasedVersion = 1
  _Version = 1
FEATURE [PartDesign::Pocket] Pocket009
  AddSubType = 1
  AlongSketchNormal = false
  AutoTaperInnerAngle = true
  BaseFeature = -> Pocket008
  CheckUpToFaceLimits = true
  ClaimChildren = false
  Direction = (-1e-16,-1,2e-16)
  Fit = 0
  FitJoin = 0
  InnerFit = 0
  InnerFitJoin = 0
  InvalidShape = false
  Length = 3
  Length2 = 10
  Linearize = true
  NewSolid = false
  Profile = -> Pocket009_Profile
  Suppress = false
  TaperInnerAngle = 0
  TaperInnerAngleRev = 0
  TreeRank = 94
  Type = 0
  ValidateShape = true
  _ProfileBasedVersion = 1
  _Version = 1
FEATURE [PartDesign::Pocket] Pocket010  label="BottomCase"
  AddSubType = 1
  AlongSketchNormal = false
  AutoTaperInnerAngle = true
  BaseFeature = -> Pocket009
  CheckUpToFaceLimits = true
  ClaimChildren = false
  Direction = (-1e-16,-1,2e-16)
  Fit = 0
  FitJoin = 0
  InnerFit = 0
  InnerFitJoin = 0
  InvalidShape = false
  Length = 4
  Length2 = 10
  Linearize = true
  Midplane = true
  NewSolid = false
  Profile = -> Pocket010_Profile
  Suppress = false
  TaperInnerAngle = 0
  TaperInnerAngleRev = 0
  TreeRank = 95
  Type = 0
  ValidateShape = true
  _ProfileBasedVersion = 1
  _Version = 1
FEATURE [Sketcher::SketchObject] Sketch013
  ArcFitTolerance = 1e-06
  AttachmentSupport = -> [Pocket010,DatumPlane001]
  ExternalBSplineMaxDegree = 5
  ExternalBSplineTolerance = 0.0001
  ExternalGeometry = -> [Pocket010]
  FullyConstrained = true
  InternalTolerance = 1e-06
  InvalidShape = false
  MakeInternals = false
  MapMode = 5
  Placement = pos=(-7.5e-15,0,34) rot=(0,0,1;0rad)
  Support = -> [Pocket010,DatumPlane001]
  TreeRank = 96
  ValidateShape = false
FEATURE [PartDesign::Plane] DatumPlane001
  AttachmentSupport = -> [Pocket010]
  InvalidShape = false
  Length = 119.306
  MapMode = 5
  MinimumLength = 10
  MinimumWidth = 10
  Placement = pos=(-7.5e-15,-1.51e-14,34) rot=(0,0,1;0rad)
  ResizeMode = 0
  Support = -> [Pocket010]
  TreeRank = 97
  ValidateShape = false
  Width = 112.306
FEATURE [PartDesign::Pad] Pad007  label="bottom_projection"
  AddSubType = 0
  AlongSketchNormal = false
  AutoTaperInnerAngle = true
  CheckUpToFaceLimits = true
  ClaimChildren = false
  Direction = (-2e-16,0,1)
  Fit = 0
  FitJoin = 0
  InnerFit = 0
  InnerFitJoin = 0
  InvalidShape = false
  Length = 3
  Length2 = 10
  Linearize = true
  NewSolid = true
  Profile = -> Sketch013
  ReferenceAxis = -> Sketch013 [N_Axis]
  Suppress = false
  TaperInnerAngle = 0
  TaperInnerAngleRev = 0
  TreeRank = 98
  Type = 0
  ValidateShape = true
  _ProfileBasedVersion = 1
FEATURE [PartDesign::Boolean] Boolean  label="TopCase"
  BaseFeature = -> Pad007
  ClaimAllChildren = false
  ExportMode = 0
  Group = -> [Reference,Reference001,Reference002,Reference003]
  InvalidShape = false
  NewSolid = false
  Suppress = false
  TreeRank = 132
  Type = 1
  ValidateShape = true
  _ExportChildren = -> [Reference,Reference001,Reference002,Reference003]
  _GroupVersion = 1
FEATURE [PartDesign::Boolean] Boolean001
  BaseFeature = -> Pocket005
  ClaimAllChildren = false
  ExportMode = 0
  Group = -> [Reference004,Reference005,Reference006,Reference007]
  InvalidShape = false
  NewSolid = false
  Suppress = false
  TreeRank = 141
  Type = 1
  ValidateShape = true
  _ExportChildren = -> [Reference004,Reference005,Reference006,Reference007]
  _GroupVersion = 1
FEATURE [Sketcher::SketchObject] Sketch014
  ArcFitTolerance = 1e-06
  AttachmentSupport = -> [Pocket010]
  ExternalBSplineMaxDegree = 5
  ExternalBSplineTolerance = 0.0001
  ExternalGeometry = -> [Pocket010]
  FullyConstrained = true
  InternalTolerance = 1e-06
  InvalidShape = false
  MakeInternals = false
  MapMode = 5
  Placement = pos=(0,0,5) rot=(0,0,1;0rad)
  Support = -> [Pocket010]
  TreeRank = 150
  ValidateShape = false
  sketch-geometry (7):
    g0: Circle CenterX=-44 CenterY=-29.5 CenterZ=0 NormalX=0 NormalY=0 NormalZ=1 AngleXU=0 Radius=1.45
    g1: Circle CenterX=-44 CenterY=21.5 CenterZ=0 NormalX=0 NormalY=0 NormalZ=1 AngleXU=0 Radius=1.45
    g2: Circle CenterX=-10 CenterY=-36.5 CenterZ=0 NormalX=0 NormalY=0 NormalZ=1 AngleXU=0 Radius=1.45
    g3: Circle CenterX=44 CenterY=-25.5 CenterZ=0 NormalX=0 NormalY=0 NormalZ=1 AngleXU=0 Radius=1.45
    g4: Circle CenterX=44 CenterY=28.5 CenterZ=0 NormalX=0 NormalY=0 NormalZ=1 AngleXU=0 Radius=1.45
    g5: LineSegment [constr] StartX=-44 StartY=-29.5 StartZ=0 EndX=-44 EndY=21.5 EndZ=0
    g6: LineSegment [constr] StartX=44 StartY=-25.5 StartZ=0 EndX=44 EndY=28.5 EndZ=0
  constraints (19):
    c: Equal(g0,g1)
    c: Equal(g1,g2)
    c: Equal(g2,g3)
    c: Equal(g3,g4)
    c: Coincident(g5,g0)
    c: Coincident(g5,g1)
    c: Vertical(g5)
    c: Coincident(g6,g3)
    c: Coincident(g6,g4)
    c: Vertical(g6)
    c: DistanceY(g0,g-3) = 76
    c: DistanceX(g-3,g0) = 6
    c: DistanceY(g1,g-3) = 25
    c: DistanceY(g2,g-3) = 83
    c: DistanceX(g-3,g2) = 40
    c: DistanceY(g3,g-3) = 72
    c: DistanceY(g4,g-3) = 18
    c: DistanceX(g-3,g4) = 94
    c: Diameter(g3) = 2.9
FEATURE [PartDesign::Pocket] Pocket011
  AddSubType = 1
  AlongSketchNormal = false
  AutoTaperInnerAngle = true
  BaseFeature = -> Pad008
  CheckUpToFaceLimits = true
  ClaimChildren = false
  Direction = (0,0,-1)
  Fit = 0
  FitJoin = 0
  InnerFit = 0
  InnerFitJoin = 0
  InvalidShape = false
  Length = 4
  Length2 = 10
  Linearize = true
  NewSolid = false
  Profile = -> Sketch014
  ReferenceAxis = -> Sketch014 [N_Axis]
  Suppress = false
  TaperInnerAngle = 0
  TaperInnerAngleRev = 0
  TreeRank = 151
  Type = 0
  ValidateShape = true
  _ProfileBasedVersion = 1
  _Version = 1
FEATURE [PartDesign::Pad] Pad008
  AddSubType = 0
  AlongSketchNormal = false
  AutoTaperInnerAngle = true
  BaseFeature = -> Pocket010
  CheckUpToFaceLimits = true
  ClaimChildren = false
  Direction = (0,0,1)
  Fit = 0
  FitJoin = 0
  InnerFit = 0
  InnerFitJoin = 0
  InvalidShape = false
  Length = 2
  Length2 = 10
  Linearize = true
  NewSolid = false
  Profile = -> Pocket010 [Edge1343,Edge1458,Edge17,Edge1432,Edge1322,Edge1435,Edge12,Edge1412,Edge1305,Edge1408,Edge6,Edge1413,Edge1309,Edge1417,Edge22,Edge1462]
  Suppress = false
  TaperInnerAngle = 0
  TaperInnerAngleRev = 0
  TreeRank = 152
  Type = 0
  ValidateShape = true
  _ProfileBasedVersion = 1
note: 5 file-system paths scrubbed to <path> (originals preserved in the JSON sidecar)
